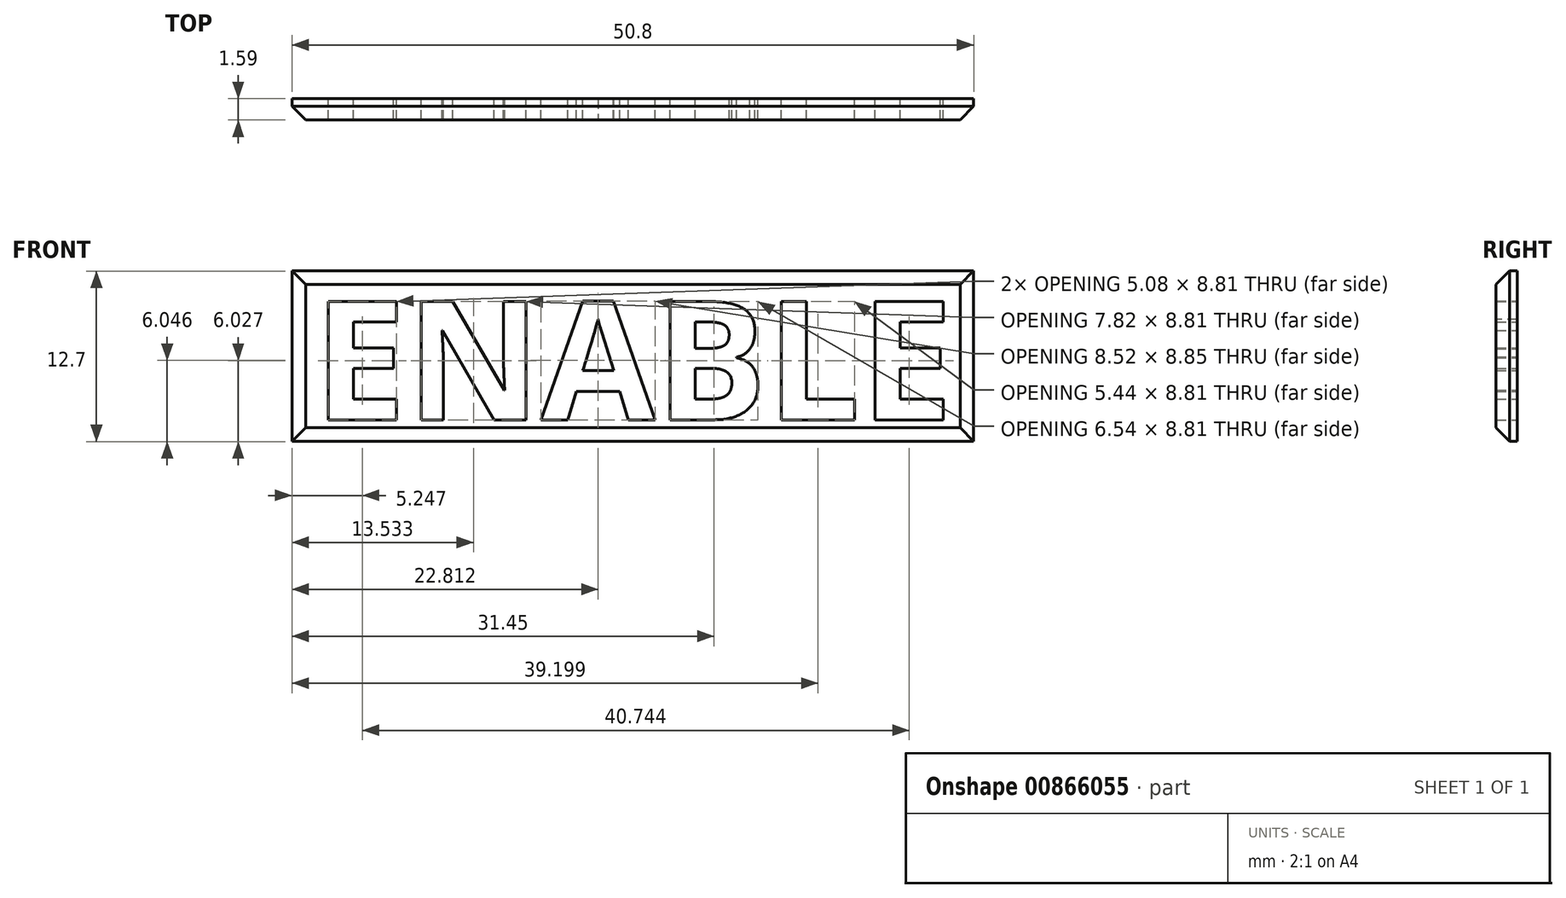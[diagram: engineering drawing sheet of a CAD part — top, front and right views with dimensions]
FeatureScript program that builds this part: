
annotation { "Feature Type Name" : "Feature", "Feature Type Description" : "" }
export const myFeature = defineFeature(function(context is Context, id is Id, definition is map)
    precondition{}
    {
        {
            var Q0;
            Q0=qCreatedBy(makeId("Front.planeOp"),FACE);
            var sketch = newSketch(context, id + "F0", { "sketchPlane" : qUnion([Q0])});
            skLineSegment(sketch, "E0.bottom", {"start": v(-34.56, 16.68) * mm, "end": v(16.24, 16.68) * mm});
            skLineSegment(sketch, "E0.top", {"start": v(-34.56, 3.98) * mm, "end": v(16.24, 3.98) * mm});
            skLineSegment(sketch, "E0.left", {"start": v(-34.56, 16.68) * mm, "end": v(-34.56, 3.98) * mm});
            skLineSegment(sketch, "E0.right", {"start": v(16.24, 16.68) * mm, "end": v(16.24, 3.98) * mm});
            skText(sketch, "E1", { "text": "ENABLE", "fontName": "OpenSans-Bold.ttf"});
            const initialGuessF0  = {"E1": [-0.03296, 0.0056, 1, 0, 0.00889]};
            skSetInitialGuess(sketch, initialGuessF0);
            skSolve(sketch);
        }
        {
            var Q0;
            Q0=makeQuery(id+"F0.imprint","IMPRINT",FACE,{"disambiguationData":[TD([[makeQuery(id+"F0.imprint","IMPRINT",EDGE,{"derivedFrom":sQuery(id+"F0.wireOp",EDGE,"E0.bottom")}),-1.0]])]});
            var Q1;
            Q1=makeQuery(id+"F0.imprint","IMPRINT",FACE,{"disambiguationData":[TD([[makeQuery(id+"F0.imprint","IMPRINT",EDGE,{"derivedFrom":sQuery(id+"F0.wireOp",EDGE,"E1.sketch_text.stroke-66")}),1.0]])]});
            var Q2;
            Q2=makeQuery(id+"F0.imprint","IMPRINT",FACE,{"disambiguationData":[TD([[makeQuery(id+"F0.imprint","IMPRINT",EDGE,{"derivedFrom":sQuery(id+"F0.wireOp",EDGE,"E1.sketch_text.stroke-60")}),1.0]])]});
            var Q3;
            Q3=makeQuery(id+"F0.imprint","IMPRINT",FACE,{"disambiguationData":[TD([[makeQuery(id+"F0.imprint","IMPRINT",EDGE,{"derivedFrom":sQuery(id+"F0.wireOp",EDGE,"E1.sketch_text.stroke-34")}),1.0]])]});
            var Q4;
            Q4=makeQuery(id+"F0.imprint","IMPRINT",FACE,{"disambiguationData":[TD([[makeQuery(id+"F0.imprint","IMPRINT",EDGE,{"derivedFrom":sQuery(id+"F0.wireOp",EDGE,"E1.sketch_text.stroke-50")}),1.0]])]});
            extrude(context, id + "F1", {"entities" : qUnion([Q0, Q1, Q2, Q3, Q4]), "depth" : 1.59 * mm, "offsetDistance" : 25.4 * mm});
        }
        {
            var Q0;
            Q0=makeQuery(id+"F1.opExtrude","CAP_EDGE",EDGE,{"disambiguationData":[OSD([sQuery(id+"F0.wireOp",EDGE,"E0.top")])],"isStart":false});
            var Q1;
            Q1=makeQuery(id+"F1.opExtrude","CAP_EDGE",EDGE,{"disambiguationData":[OSD([sQuery(id+"F0.wireOp",EDGE,"E0.left")])],"isStart":false});
            var Q2;
            Q2=makeQuery(id+"F1.opExtrude","CAP_EDGE",EDGE,{"disambiguationData":[OSD([sQuery(id+"F0.wireOp",EDGE,"E0.bottom")])],"isStart":false});
            var Q3;
            Q3=makeQuery(id+"F1.opExtrude","CAP_EDGE",EDGE,{"disambiguationData":[OSD([sQuery(id+"F0.wireOp",EDGE,"E0.right")])],"isStart":false});
            chamfer(context, id + "F2", {"entities" : qUnion([Q0, Q1, Q2, Q3]), "width" : 1.02 * mm, "tangentPropagation" : true});
        }
    });
